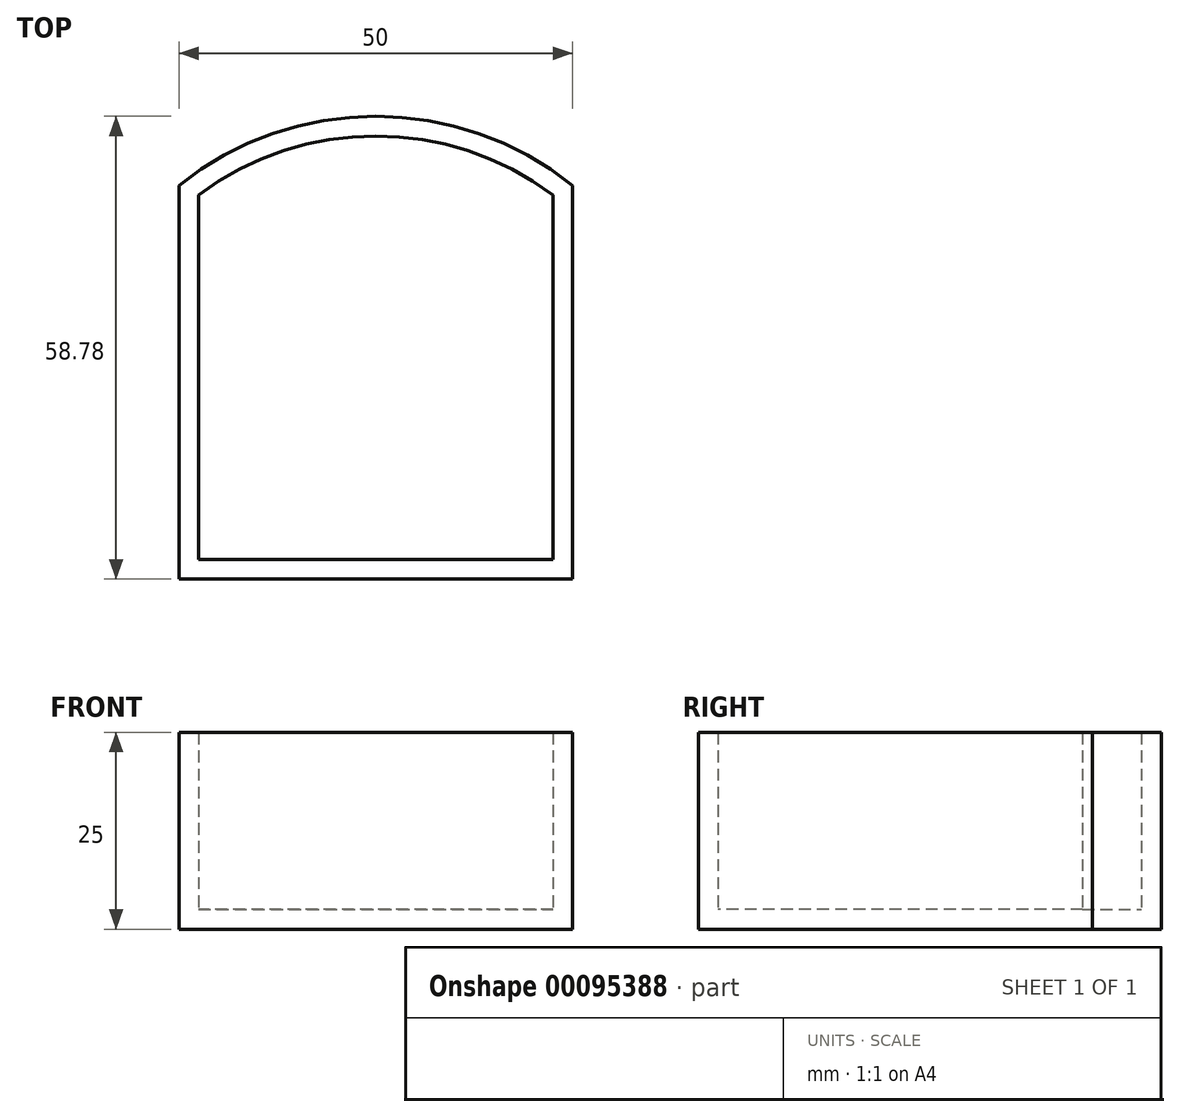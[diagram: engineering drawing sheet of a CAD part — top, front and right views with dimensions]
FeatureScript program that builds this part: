
annotation { "Feature Type Name" : "Feature", "Feature Type Description" : "" }
export const myFeature = defineFeature(function(context is Context, id is Id, definition is map)
    precondition{}
    {
        {
            var Q0;
            Q0=qCreatedBy(makeId("Top.planeOp"),FACE);
            var sketch = newSketch(context, id + "F0", { "sketchPlane" : qUnion([Q0])});
            skLineSegment(sketch, "E0.bottom", {"start": v(-25, 25) * mm, "end": v(25, 25) * mm});
            skLineSegment(sketch, "E0.top", {"start": v(-25, -25) * mm, "end": v(25, -25) * mm});
            skLineSegment(sketch, "E0.left", {"start": v(-25, 25) * mm, "end": v(-25, -25) * mm});
            skLineSegment(sketch, "E0.right", {"start": v(25, 25) * mm, "end": v(25, -25) * mm});
            skPoint(sketch, "E0.middle", {"position": v(0, 0) * mm});
            skArc(sketch, "E1", {"start": v(25, 25) * mm, "mid": v(0, 33.78) * mm, "end": v(-25, 25) * mm});
            skSolve(sketch);
        }
        {
            var Q0;
            Q0 = qSketchRegion(id + "F0", true);
            extrude(context, id + "F1", {"entities" : qUnion([Q0]), "depth" : 25 * mm});
        }
        {
            var Q0;
            Q0=makeQuery(id+"F1.opExtrude","CAP_FACE",FACE,{"disambiguationData":[OSD([sQuery(id+"F0.wireOp",EDGE,"E0.top"),sQuery(id+"F0.wireOp",EDGE,"E0.left"),sQuery(id+"F0.wireOp",EDGE,"E0.right"),sQuery(id+"F0.wireOp",EDGE,"E1")])],"isStart":false});
            shell(context, id + "F2", {"entities" : qUnion([Q0]), "thickness" : 2.5 * mm});
        }
    });
